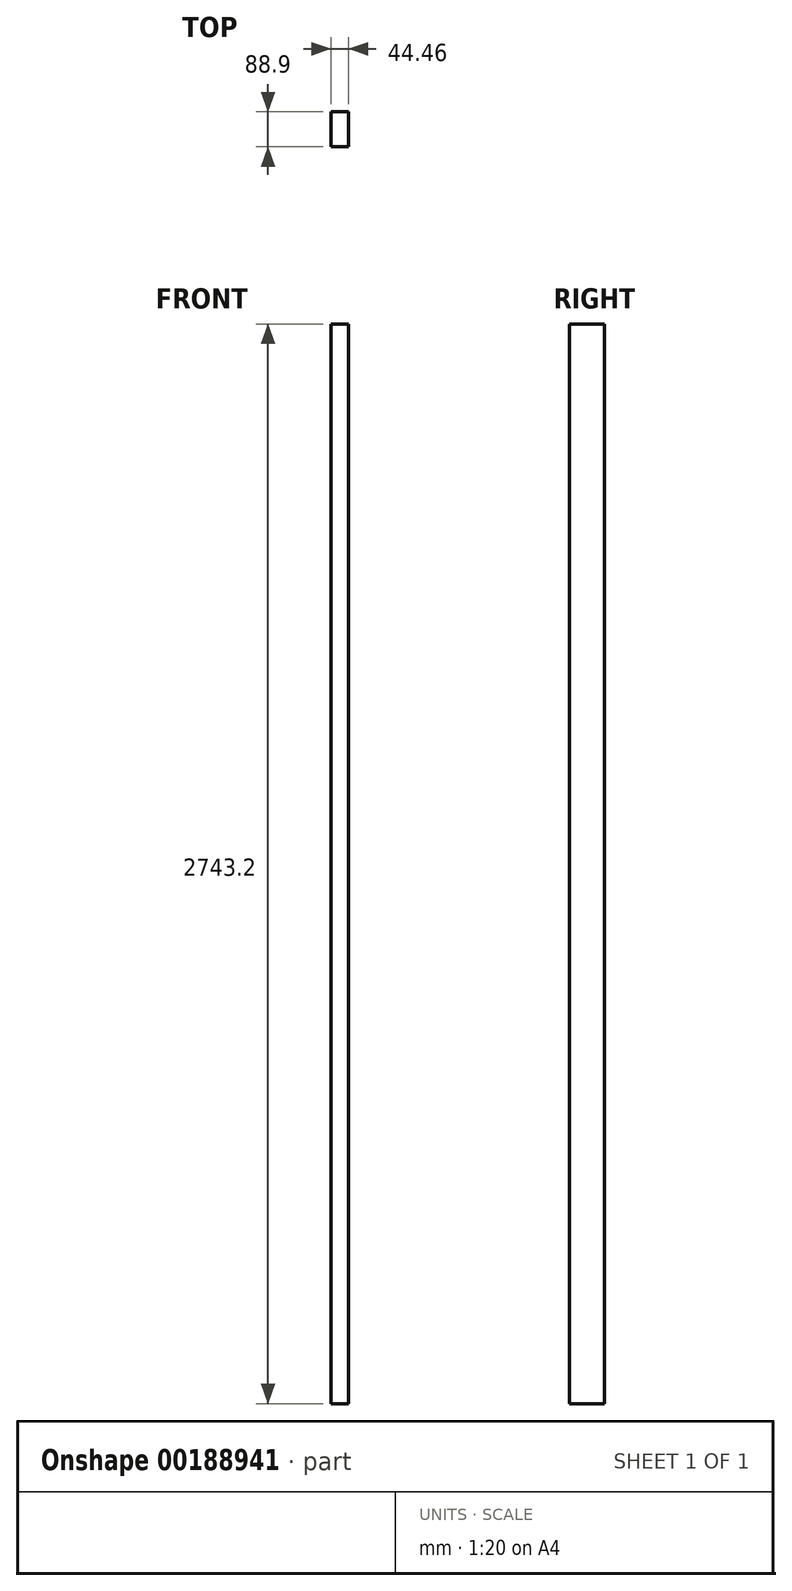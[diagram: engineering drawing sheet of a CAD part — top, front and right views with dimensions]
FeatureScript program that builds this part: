
annotation { "Feature Type Name" : "Feature", "Feature Type Description" : "" }
export const myFeature = defineFeature(function(context is Context, id is Id, definition is map)
    precondition{}
    {
        {
            var Q0;
            Q0=qCreatedBy(makeId("Top.planeOp"),FACE);
            var sketch = newSketch(context, id + "F1", { "sketchPlane" : qUnion([Q0])});
            skLineSegment(sketch, "E0.bottom", {"start": v(22.23, -44.45) * mm, "end": v(-22.22, -44.45) * mm});
            skLineSegment(sketch, "E0.top", {"start": v(22.22, 44.45) * mm, "end": v(-22.23, 44.45) * mm});
            skLineSegment(sketch, "E0.left", {"start": v(22.23, -44.45) * mm, "end": v(22.22, 44.45) * mm});
            skLineSegment(sketch, "E0.right", {"start": v(-22.22, -44.45) * mm, "end": v(-22.23, 44.45) * mm});
            skPoint(sketch, "E0.middle", {"position": v(0, 0) * mm});
            skSolve(sketch);
        }
        {
            var Q0;
            Q0=makeQuery(id+"F1.imprint","IMPRINT",FACE,{"disambiguationData":[TD([[makeQuery(id+"F1.imprint","IMPRINT",EDGE,{"derivedFrom":sQuery(id+"F1.wireOp",EDGE,"E0.bottom")}),-1.0]])]});
            extrude(context, id + "F0", {"entities" : qUnion([Q0]), "endBound" : BoundingType.SYMMETRIC, "depth" : 2743.2 * mm});
        }
    });
